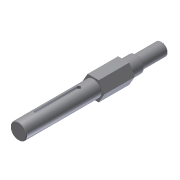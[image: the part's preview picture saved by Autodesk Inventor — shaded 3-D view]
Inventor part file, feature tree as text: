
AUTODESK INVENTOR PART (.ipt)
format: ipt  version: 2011 (Build 150239000, 239)  size: 107,008 bytes
history: native  units: in
note: dims shown in document units (in); Inventor stores cm internally (conversion verified against a paired STEP export)
features: chamfer x1, imported_body x1
ambient origin geometry x8: Origin, YZ Plane, XZ Plane, XY Plane, X Axis, Y Axis, Z Axis, Center Point
feature tree (2):
  chamfer  "Chamfer1"  [1 undecoded]
  imported_body  "Base1"
note: 1 required parameter value undecoded (feature->parameter linkage not recoverable at this tier; creation-order binding heuristic only, values carry confidence <= 0.55)
